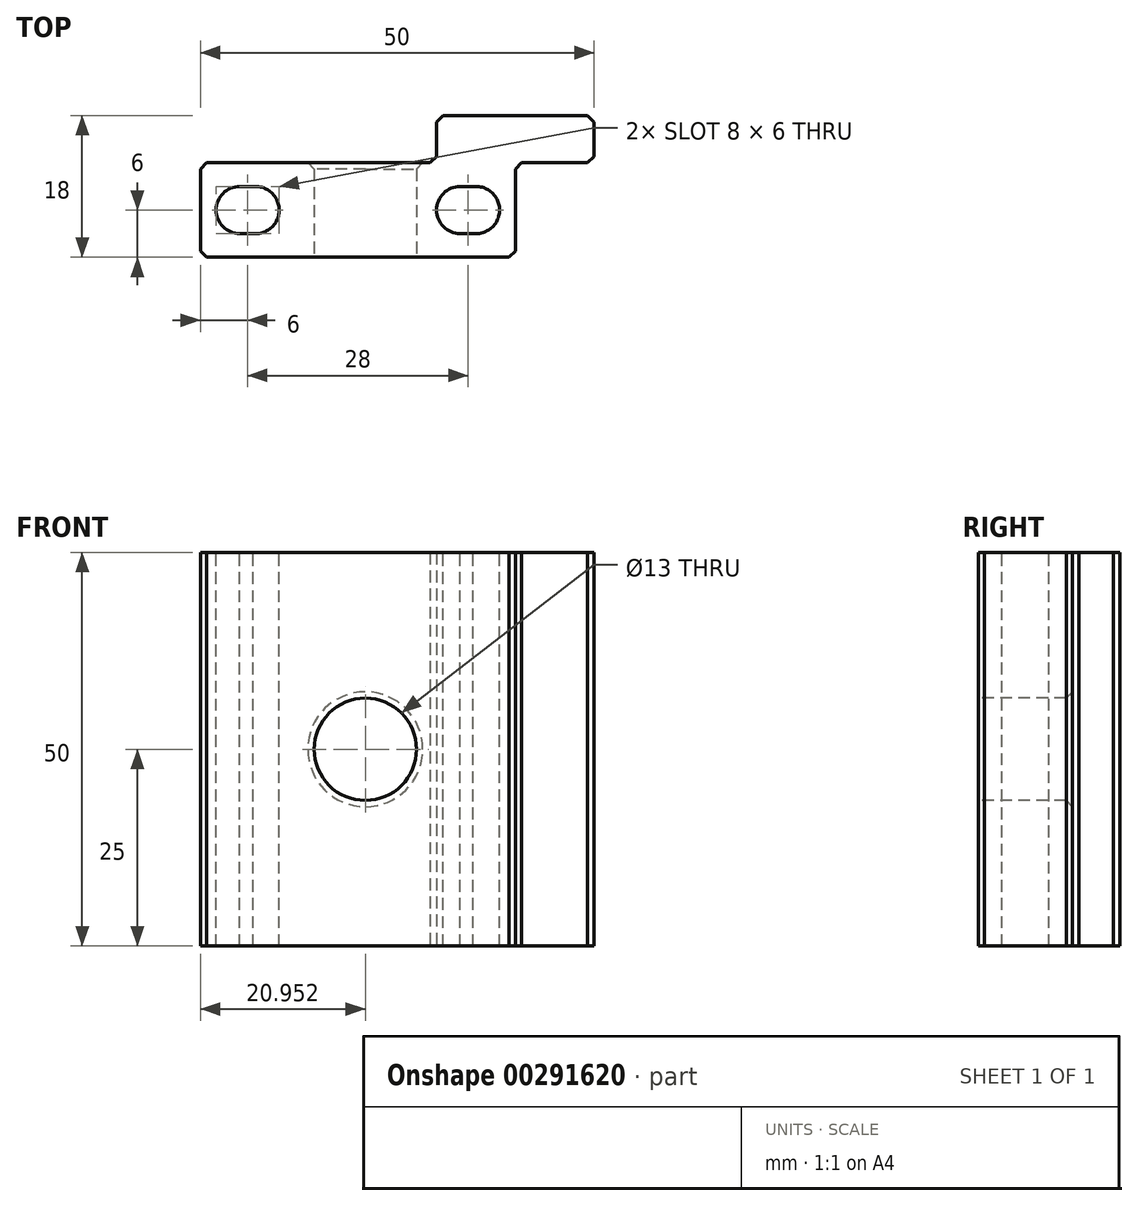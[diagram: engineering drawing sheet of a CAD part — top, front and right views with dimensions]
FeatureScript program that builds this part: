
annotation { "Feature Type Name" : "Feature", "Feature Type Description" : "" }
export const myFeature = defineFeature(function(context is Context, id is Id, definition is map)
    precondition{}
    {
        {
            var Q0;
            Q0=qCreatedBy(makeId("Top.planeOp"),FACE);
            var sketch = newSketch(context, id + "F0", { "sketchPlane" : qUnion([Q0])});
            skLineSegment(sketch, "E0", {"start": v(-32.26, 0) * mm, "end": v(-32.26, 12) * mm});
            skLineSegment(sketch, "E1", {"start": v(7.74, 0) * mm, "end": v(-32.26, 0) * mm});
            skLineSegment(sketch, "E2", {"start": v(-32.26, 12) * mm, "end": v(-2.26, 12) * mm});
            skLineSegment(sketch, "E3", {"start": v(17.74, 18) * mm, "end": v(-2.26, 18) * mm});
            skLineSegment(sketch, "E4", {"start": v(-2.26, 18) * mm, "end": v(-2.26, 12) * mm});
            skLineSegment(sketch, "E5", {"start": v(7.74, 0) * mm, "end": v(7.74, 12) * mm});
            skLineSegment(sketch, "E6", {"start": v(7.74, 12) * mm, "end": v(17.74, 12) * mm});
            skLineSegment(sketch, "E7", {"start": v(17.74, 12) * mm, "end": v(17.74, 18) * mm});
            skSolve(sketch);
        }
        {
            var Q0;
            Q0=makeQuery(id+"F0.imprint","IMPRINT",FACE,{"disambiguationData":[TD([[makeQuery(id+"F0.imprint","IMPRINT",EDGE,{"derivedFrom":sQuery(id+"F0.wireOp",EDGE,"E0")}),-1.0]])]});
            extrude(context, id + "F1", {"entities" : qUnion([Q0]), "depth" : 50 * mm});
        }
        {
            var Q0;
            Q0=makeQuery(id+"F1.opExtrude","CAP_FACE",FACE,{"disambiguationData":[OSD([sQuery(id+"F0.wireOp",EDGE,"E0"),sQuery(id+"F0.wireOp",EDGE,"o2G7Yv12-dZbw-Aksm-vXnR-qdNdU4429cXs"),sQuery(id+"F0.wireOp",EDGE,"KFIwA6Dd-c2ay-AD7S-g6iB-lHe2tFGU7Rjt"),sQuery(id+"F0.wireOp",EDGE,"hYOSYNOn-eQqk-npWH-pDCk-WvwbaqOjX2O7"),sQuery(id+"F0.wireOp",EDGE,"Nx4Z8nex-UuLY-GHDb-3vj8-En5UT6CPUsVi"),sQuery(id+"F0.wireOp",EDGE,"E1")])],"isStart":false});
            var sketch = newSketch(context, id + "F2", { "sketchPlane" : qUnion([Q0])});
            skArc(sketch, "E8", {"start": v(-27.26, 9) * mm, "mid": v(-30.26, 6) * mm, "end": v(-27.26, 3) * mm});
            skArc(sketch, "E9", {"start": v(-25.6, 3.02) * mm, "mid": v(-22.26, 5.83) * mm, "end": v(-25.26, 9) * mm});
            skLineSegment(sketch, "E10", {"start": v(-27.26, 9) * mm, "end": v(-25.26, 9) * mm});
            skLineSegment(sketch, "E11", {"start": v(-25.6, 3.02) * mm, "end": v(-27.26, 3) * mm});
            skArc(sketch, "E12.1.0.0", {"start": v(2.4, 3.02) * mm, "mid": v(5.74, 5.83) * mm, "end": v(2.74, 9) * mm});
            skLineSegment(sketch, "E12.1.0.1", {"start": v(0.74, 9) * mm, "end": v(2.74, 9) * mm});
            skArc(sketch, "E12.1.0.3", {"start": v(0.74, 9) * mm, "mid": v(-2.26, 6) * mm, "end": v(0.74, 3) * mm});
            skLineSegment(sketch, "E12.1.0.4", {"start": v(2.4, 3.02) * mm, "end": v(0.74, 3) * mm});
            skLineSegment(sketch, "E12.direction1", {"start": v(-27.26, 3) * mm, "end": v(0.74, 3) * mm, "construction": true});
            skSolve(sketch);
        }
        {
            var Q0;
            Q0=makeQuery(id+"F2.imprint","IMPRINT",FACE,{"disambiguationData":[TD([[makeQuery(id+"F2.imprint","IMPRINT",EDGE,{"derivedFrom":sQuery(id+"F2.wireOp",EDGE,"E8")}),1.0]])]});
            var Q1;
            Q1=makeQuery(id+"F2.imprint","IMPRINT",FACE,{"disambiguationData":[TD([[makeQuery(id+"F2.imprint","IMPRINT",EDGE,{"derivedFrom":sQuery(id+"F2.wireOp",EDGE,"E12.1.0.0")}),1.0]])]});
            extrude(context, id + "F3", {"entities" : qUnion([Q0, Q1]), "operationType" : NewBodyOperationType.REMOVE, "oppositeDirection" : true, "depth" : 55 * mm});
        }
        {
            var Q0;
            Q0=makeQuery(id+"F1.opExtrude","SWEPT_FACE",FACE,{"disambiguationData":[OSD([sQuery(id+"F0.wireOp",EDGE,"E1")])]});
            var sketch = newSketch(context, id + "F4", { "sketchPlane" : qUnion([Q0])});
            skCircle(sketch, "E13", {"center": v(-11.3, 25) * mm, "radius": 6.5 * mm});
            skSolve(sketch);
        }
        {
            var Q0;
            Q0=makeQuery(id+"F4.imprint","IMPRINT",FACE,{"disambiguationData":[TD([[makeQuery(id+"F4.imprint","IMPRINT",EDGE,{"derivedFrom":sQuery(id+"F4.wireOp",EDGE,"E13")}),1.0]])]});
            extrude(context, id + "F5", {"entities" : qUnion([Q0]), "operationType" : NewBodyOperationType.REMOVE, "oppositeDirection" : true, "depth" : 13 * mm});
        }
        {
            var Q0;
            Q0=makeQuery(id+"F1.opExtrude","SWEPT_EDGE",EDGE,{"disambiguationData":[OSD([sQuery(id+"F0.wireOp",EDGE,"E1"),sQuery(id+"F0.wireOp",EDGE,"E5")])]});
            var Q1;
            Q1=makeQuery(id+"F1.opExtrude","SWEPT_EDGE",EDGE,{"disambiguationData":[OSD([sQuery(id+"F0.wireOp",EDGE,"E5"),sQuery(id+"F0.wireOp",EDGE,"E6")])]});
            var Q2;
            Q2=makeQuery(id+"F1.opExtrude","SWEPT_EDGE",EDGE,{"disambiguationData":[OSD([sQuery(id+"F0.wireOp",EDGE,"E6"),sQuery(id+"F0.wireOp",EDGE,"E7")])]});
            var Q3;
            Q3=makeQuery(id+"F1.opExtrude","SWEPT_EDGE",EDGE,{"disambiguationData":[OSD([sQuery(id+"F0.wireOp",EDGE,"E3"),sQuery(id+"F0.wireOp",EDGE,"E7")])]});
            var Q4;
            Q4=makeQuery(id+"F1.opExtrude","SWEPT_EDGE",EDGE,{"disambiguationData":[OSD([sQuery(id+"F0.wireOp",EDGE,"E0"),sQuery(id+"F0.wireOp",EDGE,"E2")])]});
            var Q5;
            Q5=makeQuery(id+"F1.opExtrude","SWEPT_EDGE",EDGE,{"disambiguationData":[OSD([sQuery(id+"F0.wireOp",EDGE,"E0"),sQuery(id+"F0.wireOp",EDGE,"E1")])]});
            var Q6;
            {var subQ0=sQuery(id+"F0.wireOp",EDGE,"E4");var subQ1=sQuery(id+"F0.wireOp",EDGE,"E2");Q6=makeQuery(id+"F5.boolean.opBoolean","SPLIT",EDGE,{"disambiguationData":[TD([makeQuery(id+"F1.opExtrude","CAP_FACE",FACE,{"disambiguationData":[OSD([sQuery(id+"F0.wireOp",EDGE,"E0"),sQuery(id+"F0.wireOp",EDGE,"E1"),subQ1,sQuery(id+"F0.wireOp",EDGE,"E3"),subQ0,sQuery(id+"F0.wireOp",EDGE,"E5"),sQuery(id+"F0.wireOp",EDGE,"E6"),sQuery(id+"F0.wireOp",EDGE,"E7")])],"isStart":false})])],"derivedFrom":makeQuery(id+"F1.opExtrude","SWEPT_EDGE",EDGE,{"disambiguationData":[OSD([subQ1,subQ0])]})});}
            var Q7;
            {var subQ0=sQuery(id+"F0.wireOp",EDGE,"E4");var subQ1=sQuery(id+"F0.wireOp",EDGE,"E2");Q7=makeQuery(id+"F5.boolean.opBoolean","SPLIT",EDGE,{"disambiguationData":[TD([makeQuery(id+"F1.opExtrude","CAP_FACE",FACE,{"disambiguationData":[OSD([sQuery(id+"F0.wireOp",EDGE,"E0"),sQuery(id+"F0.wireOp",EDGE,"E1"),subQ1,sQuery(id+"F0.wireOp",EDGE,"E3"),subQ0,sQuery(id+"F0.wireOp",EDGE,"E5"),sQuery(id+"F0.wireOp",EDGE,"E6"),sQuery(id+"F0.wireOp",EDGE,"E7")])],"isStart":true})])],"derivedFrom":makeQuery(id+"F1.opExtrude","SWEPT_EDGE",EDGE,{"disambiguationData":[OSD([subQ1,subQ0])]})});}
            var Q8;
            Q8=makeQuery(id+"F1.opExtrude","SWEPT_EDGE",EDGE,{"disambiguationData":[OSD([sQuery(id+"F0.wireOp",EDGE,"E3"),sQuery(id+"F0.wireOp",EDGE,"E4")])]});
            var Q9;
            Q9=makeQuery(id+"F5.boolean.opBoolean","INTERSECT",EDGE,{"derivedFrom":[makeQuery(id+"F1.opExtrude","SWEPT_FACE",FACE,{"disambiguationData":[OSD([sQuery(id+"F0.wireOp",EDGE,"E2")])]}),makeQuery(id+"F5.opExtrude","SWEPT_FACE",FACE,{"disambiguationData":[OSD([sQuery(id+"F4.wireOp",EDGE,"E13")])]})]});
            var Q10;
            Q10=makeQuery(id+"F5.boolean.opBoolean","COPY",EDGE,{"derivedFrom":makeQuery(id+"F5.opExtrude","CAP_EDGE",EDGE,{"disambiguationData":[OSD([sQuery(id+"F4.wireOp",EDGE,"E13")])],"isStart":true})});
            chamfer(context, id + "F6", {"entities" : qUnion([Q0, Q1, Q2, Q3, Q4, Q5, Q6, Q7, Q8, Q9, Q10]), "width" : 0.8 * mm, "tangentPropagation" : true});
        }
    });
